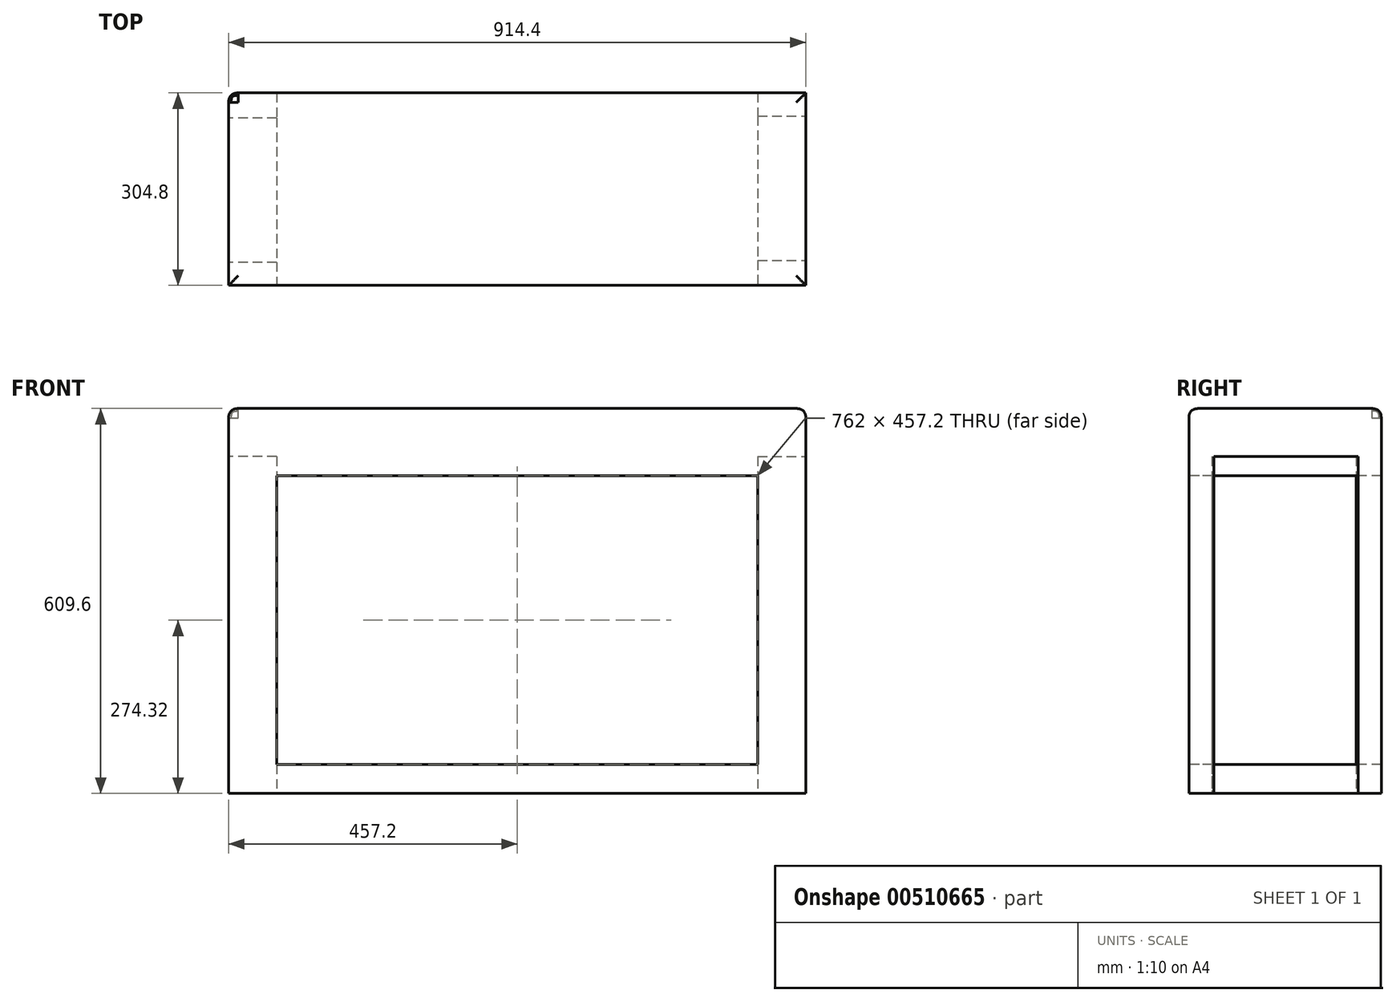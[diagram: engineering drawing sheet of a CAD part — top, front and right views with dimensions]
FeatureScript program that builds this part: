
annotation { "Feature Type Name" : "Feature", "Feature Type Description" : "" }
export const myFeature = defineFeature(function(context is Context, id is Id, definition is map)
    precondition{}
    {
        {
            var Q0;
            Q0=qCreatedBy(makeId("Top.planeOp"),FACE);
            var sketch = newSketch(context, id + "F0", { "sketchPlane" : qUnion([Q0])});
            skLineSegment(sketch, "E0.bottom", {"start": v(-434.17, 161.22) * mm, "end": v(480.23, 161.22) * mm});
            skLineSegment(sketch, "E0.top", {"start": v(-434.17, -143.58) * mm, "end": v(480.23, -143.58) * mm});
            skLineSegment(sketch, "E0.left", {"start": v(-434.17, 161.22) * mm, "end": v(-434.17, -143.58) * mm});
            skLineSegment(sketch, "E0.right", {"start": v(480.23, 161.22) * mm, "end": v(480.23, -143.58) * mm});
            skSolve(sketch);
        }
        {
            var Q0;
            Q0 = qSketchRegion(id + "F0", true);
            extrude(context, id + "F1", {"entities" : qUnion([Q0]), "depth" : 609.6 * mm, "offsetDistance" : 30.48 * mm});
        }
        {
            var Q0;
            Q0=makeQuery(id+"F1.opExtrude","SWEPT_EDGE",EDGE,{"disambiguationData":[OSD([sQuery(id+"F0.wireOp",EDGE,"E0.bottom"),sQuery(id+"F0.wireOp",EDGE,"E0.left")])]});
            var Q1;
            Q1=makeQuery(id+"F1.opExtrude","CAP_EDGE",EDGE,{"disambiguationData":[OSD([sQuery(id+"F0.wireOp",EDGE,"E0.bottom")])],"isStart":false});
            var Q2;
            Q2=makeQuery(id+"F1.opExtrude","CAP_EDGE",EDGE,{"disambiguationData":[OSD([sQuery(id+"F0.wireOp",EDGE,"E0.left")])],"isStart":false});
            var Q3;
            Q3=makeQuery(id+"F1.opExtrude","CAP_EDGE",EDGE,{"disambiguationData":[OSD([sQuery(id+"F0.wireOp",EDGE,"E0.top")])],"isStart":false});
            var Q4;
            Q4=makeQuery(id+"F1.opExtrude","CAP_EDGE",EDGE,{"disambiguationData":[OSD([sQuery(id+"F0.wireOp",EDGE,"E0.right")])],"isStart":false});
            fillet(context, id + "F2", {"entities" : qUnion([Q0, Q1, Q2, Q3, Q4]), "radius" : 15.24 * mm, "tangentPropagation" : true, "rho" : 0.5, "crossSection" : FilletCrossSection.CONIC, "allowEdgeOverflow" : false});
        }
        {
            var Q0;
            Q0=makeQuery(id+"F1.opExtrude","SWEPT_FACE",FACE,{"disambiguationData":[OSD([sQuery(id+"F0.wireOp",EDGE,"E0.top")])]});
            var sketch = newSketch(context, id + "F3", { "sketchPlane" : qUnion([Q0])});
            skLineSegment(sketch, "E1.bottom", {"start": v(-357.97, 502.92) * mm, "end": v(404.03, 502.92) * mm});
            skLineSegment(sketch, "E1.top", {"start": v(-357.97, 45.72) * mm, "end": v(404.03, 45.72) * mm});
            skLineSegment(sketch, "E1.left", {"start": v(-357.97, 502.92) * mm, "end": v(-357.97, 45.72) * mm});
            skLineSegment(sketch, "E1.right", {"start": v(404.03, 502.92) * mm, "end": v(404.03, 45.72) * mm});
            skSolve(sketch);
        }
        {
            var Q0;
            Q0 = qSketchRegion(id + "F3", true);
            extrude(context, id + "F4", {"entities" : qUnion([Q0]), "operationType" : NewBodyOperationType.REMOVE, "oppositeDirection" : true, "depth" : 609.6 * mm, "offsetDistance" : 30.48 * mm});
        }
        {
            var Q0;
            Q0=makeQuery(id+"F1.opExtrude","SWEPT_FACE",FACE,{"disambiguationData":[OSD([sQuery(id+"F0.wireOp",EDGE,"E0.right")])]});
            var sketch = newSketch(context, id + "F5", { "sketchPlane" : qUnion([Q0])});
            skLineSegment(sketch, "E2.bottom", {"start": v(-103.96, 533.4) * mm, "end": v(124.64, 533.4) * mm});
            skLineSegment(sketch, "E2.top", {"start": v(-103.96, 0) * mm, "end": v(124.64, 0) * mm});
            skLineSegment(sketch, "E2.left", {"start": v(-103.96, 533.4) * mm, "end": v(-103.96, 0) * mm});
            skLineSegment(sketch, "E2.right", {"start": v(124.64, 533.4) * mm, "end": v(124.64, 0) * mm});
            skSolve(sketch);
        }
        {
            var Q0;
            Q0 = qSketchRegion(id + "F5", true);
            extrude(context, id + "F6", {"entities" : qUnion([Q0]), "operationType" : NewBodyOperationType.REMOVE, "oppositeDirection" : true, "depth" : 76.2 * mm, "offsetDistance" : 30.48 * mm});
        }
        {
            var Q0;
            Q0=makeQuery(id+"F1.opExtrude","SWEPT_FACE",FACE,{"disambiguationData":[OSD([sQuery(id+"F0.wireOp",EDGE,"E0.left")])]});
            var sketch = newSketch(context, id + "F7", { "sketchPlane" : qUnion([Q0])});
            skLineSegment(sketch, "E3.bottom", {"start": v(-121.6, 533.4) * mm, "end": v(107, 533.4) * mm});
            skLineSegment(sketch, "E3.top", {"start": v(-121.6, 0) * mm, "end": v(107, 0) * mm});
            skLineSegment(sketch, "E3.left", {"start": v(-121.6, 533.4) * mm, "end": v(-121.6, 0) * mm});
            skLineSegment(sketch, "E3.right", {"start": v(107, 533.4) * mm, "end": v(107, 0) * mm});
            skSolve(sketch);
        }
        {
            var Q0;
            Q0 = qSketchRegion(id + "F7", true);
            extrude(context, id + "F8", {"entities" : qUnion([Q0]), "operationType" : NewBodyOperationType.REMOVE, "oppositeDirection" : true, "depth" : 76.2 * mm, "offsetDistance" : 30.48 * mm});
        }
    });
